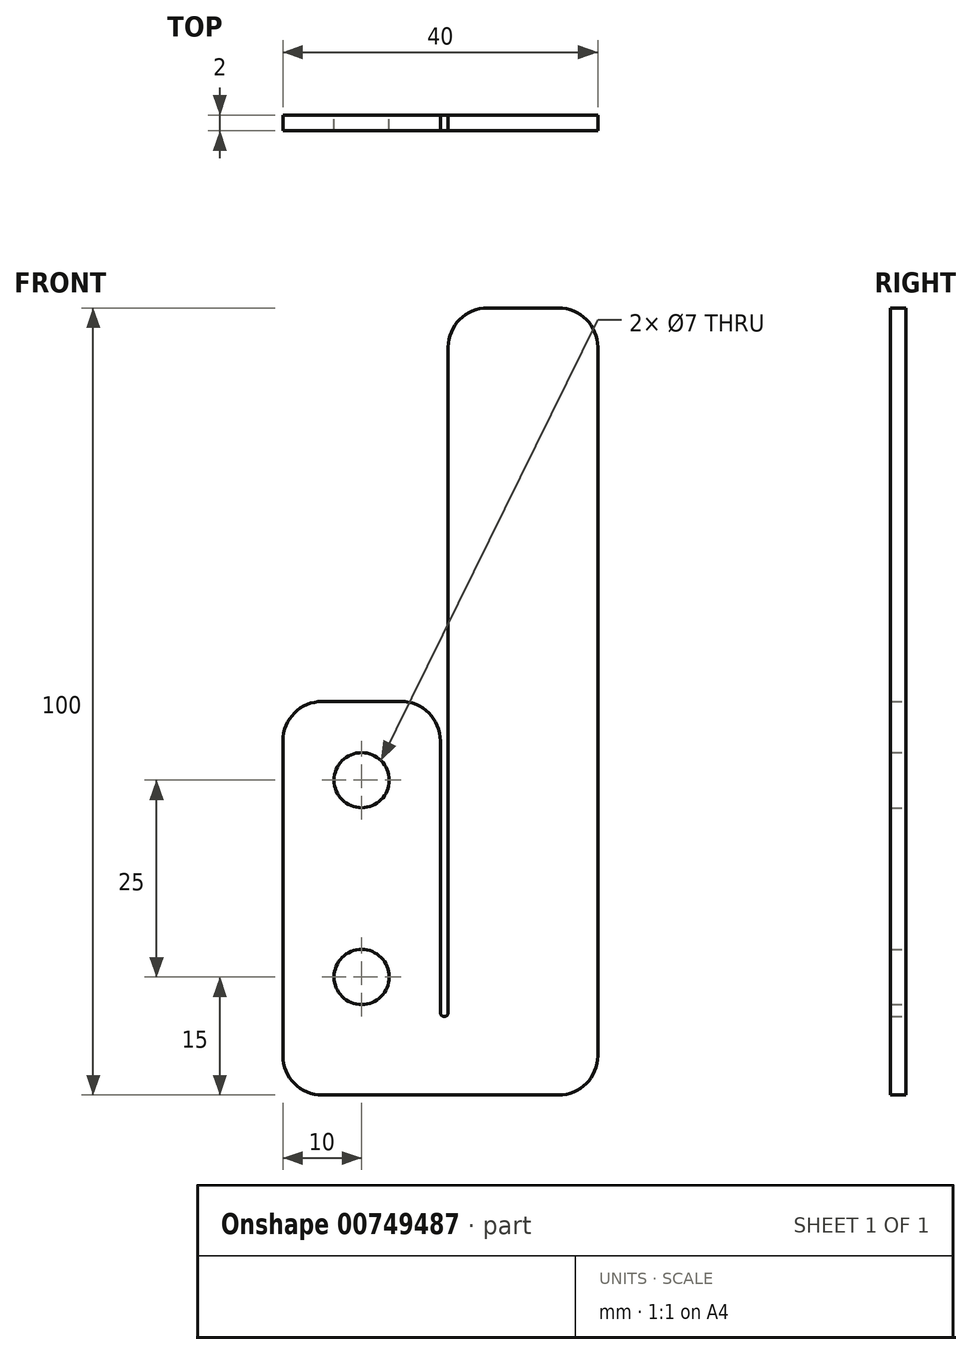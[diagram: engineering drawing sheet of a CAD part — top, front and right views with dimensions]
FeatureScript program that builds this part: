
annotation { "Feature Type Name" : "Feature", "Feature Type Description" : "" }
export const myFeature = defineFeature(function(context is Context, id is Id, definition is map)
    precondition{}
    {
        {
            var Q0;
            Q0=qCreatedBy(makeId("Front.planeOp"), FACE);
            var sketch = newSketch(context, id + "F0", { "sketchPlane" : qUnion([Q0])});
            skLineSegment(sketch, "E0", {"start": v(0, 5) * mm, "end": v(0, 45) * mm});
            skLineSegment(sketch, "E1", {"start": v(5, 50) * mm, "end": v(15, 50) * mm});
            skLineSegment(sketch, "E2", {"start": v(20, 45) * mm, "end": v(20, 10.5) * mm});
            skLineSegment(sketch, "E3", {"start": v(20.5, 10) * mm, "end": v(20.5, 10) * mm});
            skLineSegment(sketch, "E4", {"start": v(21, 10.5) * mm, "end": v(21, 95) * mm});
            skLineSegment(sketch, "E5", {"start": v(26, 100) * mm, "end": v(35, 100) * mm});
            skLineSegment(sketch, "E6", {"start": v(40, 95) * mm, "end": v(40, 5) * mm});
            skLineSegment(sketch, "E7", {"start": v(35, 0) * mm, "end": v(5, 0) * mm});
            skPoint(sketch, "E8.visualSharp", {"position": v(21, 100) * mm});
            skArc(sketch, "E8.filletArc", {"start": v(26, 100) * mm, "mid": v(22.46, 98.54) * mm, "end": v(21, 95) * mm});
            skPoint(sketch, "E9.visualSharp", {"position": v(40, 100) * mm});
            skArc(sketch, "E9.filletArc", {"start": v(40, 95) * mm, "mid": v(38.54, 98.54) * mm, "end": v(35, 100) * mm});
            skPoint(sketch, "E10.visualSharp", {"position": v(20, 50) * mm});
            skArc(sketch, "E10.filletArc", {"start": v(20, 45) * mm, "mid": v(18.54, 48.54) * mm, "end": v(15, 50) * mm});
            skPoint(sketch, "E11.visualSharp", {"position": v(0, 50) * mm});
            skArc(sketch, "E11.filletArc", {"start": v(5, 50) * mm, "mid": v(1.46, 48.54) * mm, "end": v(0, 45) * mm});
            skPoint(sketch, "E12.visualSharp", {"position": v(0, 0) * mm});
            skArc(sketch, "E12.filletArc", {"start": v(0, 5) * mm, "mid": v(1.46, 1.46) * mm, "end": v(5, 0) * mm});
            skPoint(sketch, "E13.visualSharp", {"position": v(40, 0) * mm});
            skArc(sketch, "E13.filletArc", {"start": v(35, 0) * mm, "mid": v(38.54, 1.46) * mm, "end": v(40, 5) * mm});
            skCircle(sketch, "E14", {"center": v(10, 40) * mm, "radius": 3.5 * mm});
            skCircle(sketch, "E15", {"center": v(10, 15) * mm, "radius": 3.5 * mm});
            skPoint(sketch, "E16.visualSharp", {"position": v(20, 10) * mm});
            skArc(sketch, "E16.filletArc", {"start": v(20, 10.5) * mm, "mid": v(20.15, 10.15) * mm, "end": v(20.5, 10) * mm});
            skPoint(sketch, "E17.visualSharp", {"position": v(21, 10) * mm});
            skArc(sketch, "E17.filletArc", {"start": v(20.5, 10) * mm, "mid": v(20.85, 10.15) * mm, "end": v(21, 10.5) * mm});
            skSolve(sketch);
        }
        {
            var Q0;
            Q0 = qSketchRegion(id + "F0", true);
            extrude(context, id + "F1", {"entities" : qUnion([Q0]), "depth" : 2 * mm, "offsetDistance" : 25 * mm});
        }
    });
